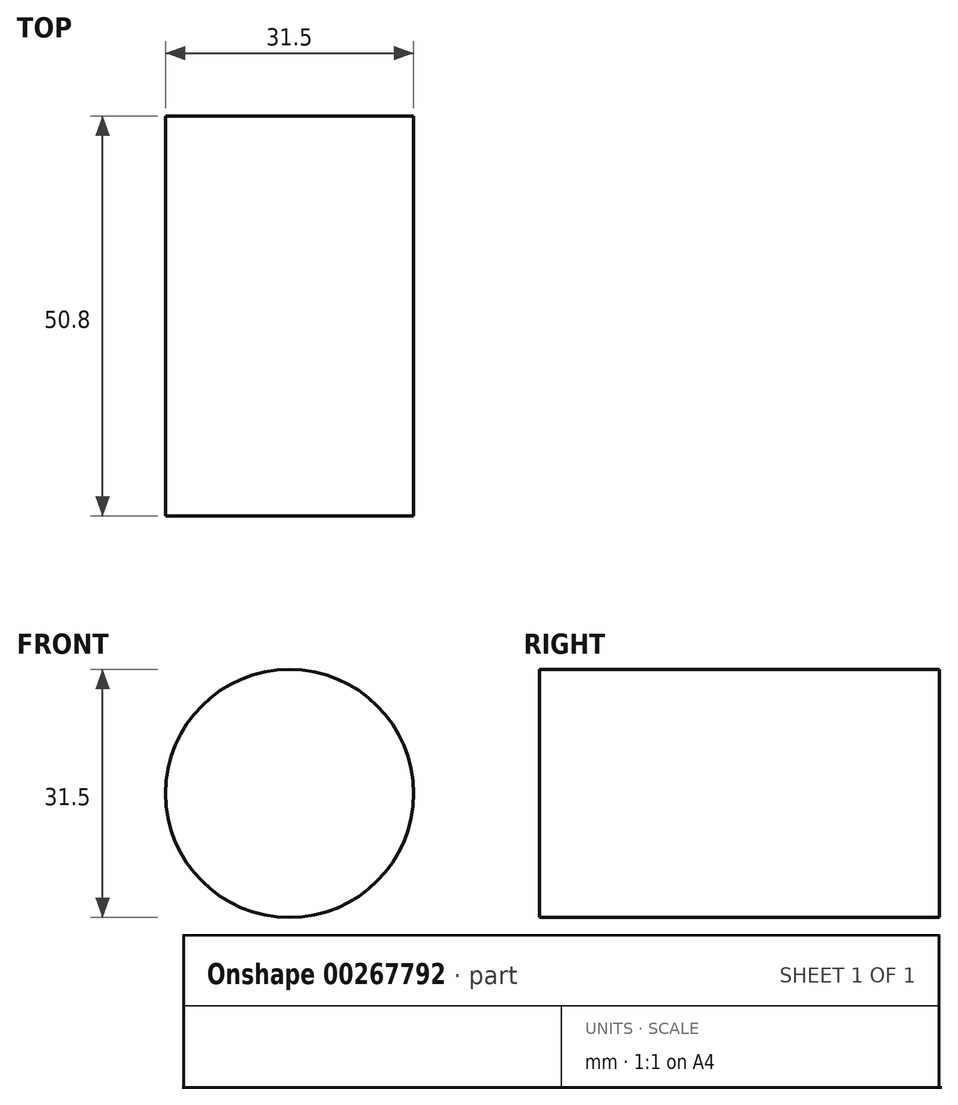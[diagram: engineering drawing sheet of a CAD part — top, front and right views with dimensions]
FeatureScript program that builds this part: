
annotation { "Feature Type Name" : "Feature", "Feature Type Description" : "" }
export const myFeature = defineFeature(function(context is Context, id is Id, definition is map)
    precondition{}
    {
        {
            var Q0;
            Q0=qCreatedBy(makeId("Front.planeOp"),FACE);
            var sketch = newSketch(context, id + "F0", { "sketchPlane" : qUnion([Q0])});
            skCircle(sketch, "E0", {"center": v(0, 0) * mm, "radius": 15.75 * mm});
            skSolve(sketch);
        }
        {
            var Q0;
            Q0=makeQuery(id+"F0.imprint","IMPRINT",FACE,{"disambiguationData":[TD([[makeQuery(id+"F0.imprint","IMPRINT",EDGE,{"derivedFrom":sQuery(id+"F0.wireOp",EDGE,"E0")}),1.0]])]});
            extrude(context, id + "F1", {"entities" : qUnion([Q0]), "depth" : 50.8 * mm});
        }
    });
